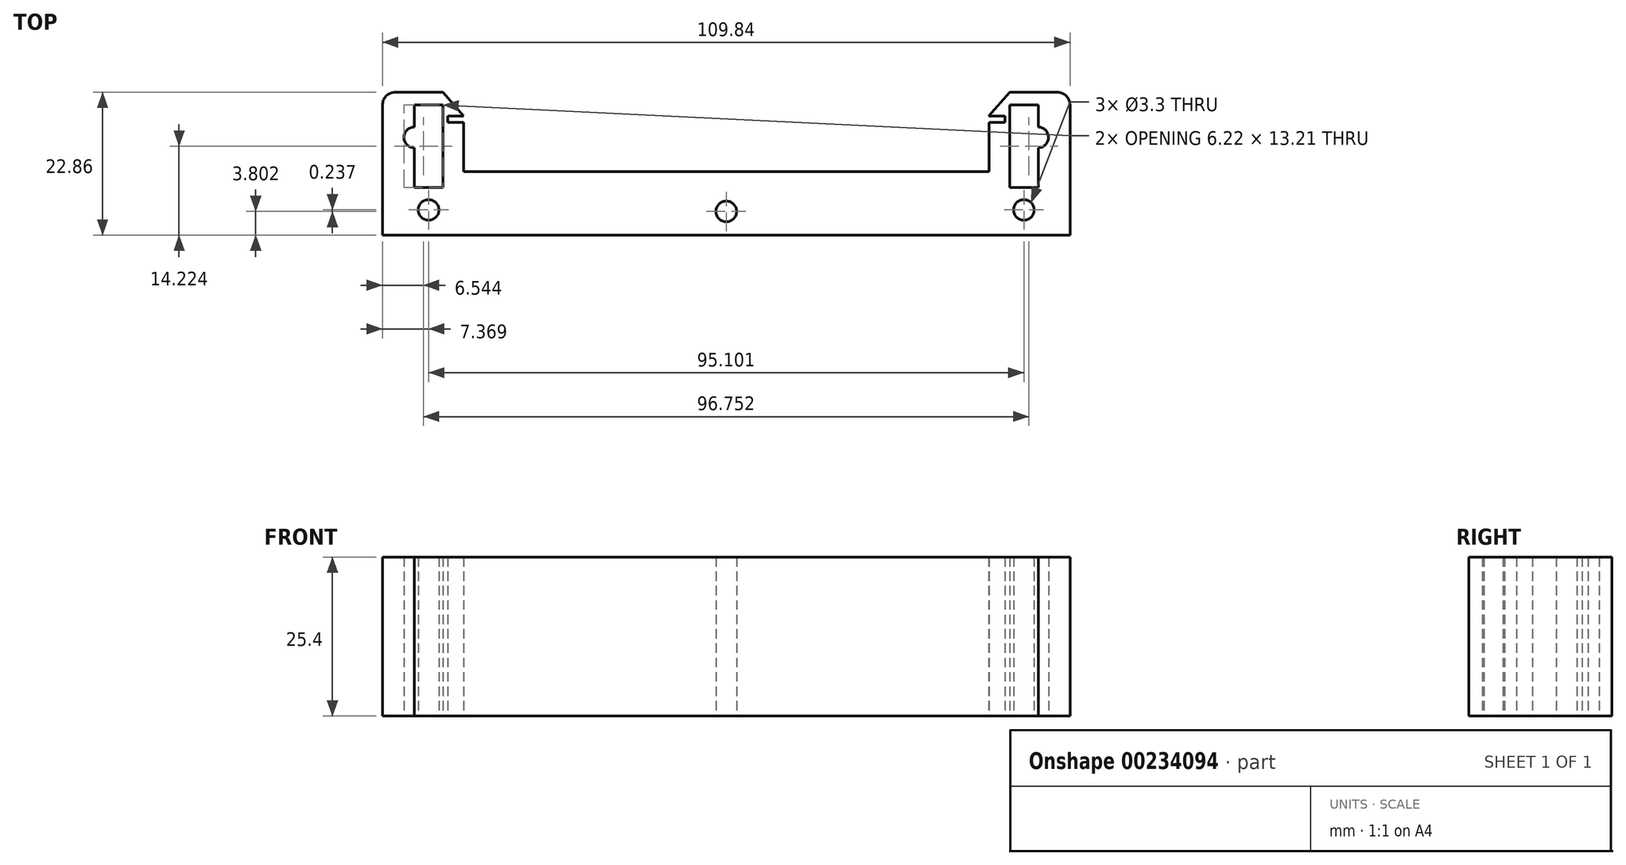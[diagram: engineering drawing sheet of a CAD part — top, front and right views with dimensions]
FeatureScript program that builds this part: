
annotation { "Feature Type Name" : "Feature", "Feature Type Description" : "" }
export const myFeature = defineFeature(function(context is Context, id is Id, definition is map)
    precondition{}
    {
        {
            var Q0;
            Q0=qCreatedBy(makeId("Top.planeOp"),FACE);
            var sketch = newSketch(context, id + "F0", { "sketchPlane" : qUnion([Q0])});
            skLineSegment(sketch, "E0.bottom", {"start": v(-49.84, -11.43) * mm, "end": v(49.84, -11.43) * mm});
            skLineSegment(sketch, "E0.top", {"start": v(-49.84, -19.05) * mm, "end": v(49.84, -19.05) * mm});
            skLineSegment(sketch, "E0.left", {"start": v(-49.84, -11.43) * mm, "end": v(-49.84, -19.05) * mm});
            skLineSegment(sketch, "E1.bottom", {"start": v(-49.84, -11.43) * mm, "end": v(-45.26, -11.43) * mm});
            skLineSegment(sketch, "E1.left", {"start": v(-49.84, -11.43) * mm, "end": v(-49.84, 1.78) * mm});
            skLineSegment(sketch, "E1.right", {"start": v(-45.26, -11.43) * mm, "end": v(-45.26, 3.8) * mm});
            skLineSegment(sketch, "E2.top", {"start": v(-45.26, 0) * mm, "end": v(-41.95, 0) * mm});
            skLineSegment(sketch, "E2.left", {"start": v(-45.26, 3.8) * mm, "end": v(-45.26, 0) * mm});
            skLineSegment(sketch, "E3.bottom", {"start": v(-45.26, -1) * mm, "end": v(-41.96, -1) * mm});
            skLineSegment(sketch, "E3.top", {"start": v(-45.26, -11.43) * mm, "end": v(-41.96, -11.43) * mm});
            skLineSegment(sketch, "E3.left", {"start": v(-45.26, -1) * mm, "end": v(-45.26, -11.43) * mm});
            skLineSegment(sketch, "E3.right", {"start": v(-41.96, -1) * mm, "end": v(-41.96, -11.43) * mm});
            skLineSegment(sketch, "E4", {"start": v(-45.26, 3.8) * mm, "end": v(-41.95, 0) * mm});
            skLineSegment(sketch, "E5.MirrorCS", {"start": v(45.26, -11.43) * mm, "end": v(41.96, -11.43) * mm});
            skLineSegment(sketch, "E6.MirrorCS", {"start": v(41.96, -1) * mm, "end": v(41.96, -11.43) * mm});
            skLineSegment(sketch, "E7.MirrorCS", {"start": v(45.26, -1) * mm, "end": v(41.96, -1) * mm});
            skLineSegment(sketch, "E8.MirrorCS", {"start": v(45.26, -1) * mm, "end": v(45.26, -11.43) * mm});
            skLineSegment(sketch, "E9.MirrorCS", {"start": v(45.26, 0) * mm, "end": v(41.95, 0) * mm});
            skLineSegment(sketch, "E10.MirrorCS", {"start": v(45.26, 3.81) * mm, "end": v(41.95, 0) * mm});
            skLineSegment(sketch, "E11.MirrorCS", {"start": v(45.26, 3.8) * mm, "end": v(45.26, 0) * mm});
            skLineSegment(sketch, "E12.MirrorCS", {"start": v(47.8, 3.8) * mm, "end": v(45.26, 3.8) * mm});
            skLineSegment(sketch, "E13.MirrorCS", {"start": v(49.84, -11.43) * mm, "end": v(49.84, 1.78) * mm});
            skLineSegment(sketch, "E14.MirrorCS", {"start": v(45.26, -11.43) * mm, "end": v(45.26, 3.8) * mm});
            skLineSegment(sketch, "E15.MirrorCS", {"start": v(49.84, -11.43) * mm, "end": v(49.84, -19.05) * mm});
            skPoint(sketch, "E16.visualSharp", {"position": v(-49.84, 3.8) * mm});
            skPoint(sketch, "E17.visualSharp", {"position": v(49.84, 3.8) * mm});
            skCircle(sketch, "E18", {"center": v(-47.55, -15.01) * mm, "radius": 1.65 * mm});
            skPoint(sketch, "E18.centerSnap0", {"position": v(-47.55, -11.43) * mm});
            skCircle(sketch, "E19", {"center": v(-49.84, -3.42) * mm, "radius": 1.65 * mm});
            skCircle(sketch, "E20.MirrorC", {"center": v(49.84, -3.42) * mm, "radius": 1.65 * mm});
            skCircle(sketch, "E21.MirrorC", {"center": v(47.55, -15.01) * mm, "radius": 1.65 * mm});
            skCircle(sketch, "E22", {"center": v(0.01, -15.25) * mm, "radius": 1.65 * mm});
            skLineSegment(sketch, "E23.bottom", {"start": v(-49.84, 1.78) * mm, "end": v(-54.92, 1.78) * mm});
            skLineSegment(sketch, "E23.top", {"start": v(-49.84, -19.05) * mm, "end": v(-54.92, -19.05) * mm});
            skLineSegment(sketch, "E23.left", {"start": v(-49.84, 1.78) * mm, "end": v(-49.84, -19.05) * mm});
            skLineSegment(sketch, "E23.right", {"start": v(-54.92, 1.78) * mm, "end": v(-54.92, -19.05) * mm});
            skLineSegment(sketch, "E24.bottom", {"start": v(-54.92, 1.78) * mm, "end": v(-45.26, 1.78) * mm});
            skLineSegment(sketch, "E24.top", {"start": v(-52.88, 3.8) * mm, "end": v(-45.26, 3.8) * mm});
            skLineSegment(sketch, "E24.left", {"start": v(-54.92, 1.78) * mm, "end": v(-54.92, 1.78) * mm});
            skLineSegment(sketch, "E24.right", {"start": v(-45.26, 1.78) * mm, "end": v(-45.26, 3.8) * mm});
            skLineSegment(sketch, "E25.MirrorCS", {"start": v(54.92, 1.78) * mm, "end": v(54.92, -19.05) * mm});
            skLineSegment(sketch, "E26.MirrorCS", {"start": v(49.84, -19.05) * mm, "end": v(54.92, -19.05) * mm});
            skLineSegment(sketch, "E27.MirrorCS", {"start": v(54.92, 1.78) * mm, "end": v(45.26, 1.78) * mm});
            skLineSegment(sketch, "E28.MirrorCS", {"start": v(52.88, 3.8) * mm, "end": v(45.26, 3.8) * mm});
            skLineSegment(sketch, "E29.MirrorCS", {"start": v(54.92, 1.78) * mm, "end": v(54.92, 1.78) * mm});
            skLineSegment(sketch, "E30.MirrorCS", {"start": v(49.84, 1.78) * mm, "end": v(49.84, -19.05) * mm});
            skPoint(sketch, "E31.visualSharp", {"position": v(-54.92, 3.8) * mm});
            skArc(sketch, "E31.filletArc", {"start": v(-52.88, 3.8) * mm, "mid": v(-54.32, 3.21) * mm, "end": v(-54.92, 1.78) * mm});
            skPoint(sketch, "E32.visualSharp", {"position": v(54.92, 3.8) * mm});
            skArc(sketch, "E32.filletArc", {"start": v(54.92, 1.78) * mm, "mid": v(54.32, 3.21) * mm, "end": v(52.88, 3.8) * mm});
            skLineSegment(sketch, "E33.bottom", {"start": v(-41.96, -11.43) * mm, "end": v(41.96, -11.43) * mm});
            skLineSegment(sketch, "E33.top", {"start": v(-41.96, -8.89) * mm, "end": v(41.96, -8.89) * mm});
            skLineSegment(sketch, "E33.left", {"start": v(-41.96, -11.43) * mm, "end": v(-41.96, -8.89) * mm});
            skLineSegment(sketch, "E33.right", {"start": v(41.96, -11.43) * mm, "end": v(41.96, -8.89) * mm});
            skLineSegment(sketch, "E34.bottom", {"start": v(-45.26, -1) * mm, "end": v(-44.5, -1) * mm});
            skLineSegment(sketch, "E34.top", {"start": v(-45.26, 0) * mm, "end": v(-44.5, 0) * mm});
            skLineSegment(sketch, "E34.left", {"start": v(-45.26, -1) * mm, "end": v(-45.26, 0) * mm});
            skLineSegment(sketch, "E34.right", {"start": v(-44.5, -1) * mm, "end": v(-44.5, 0) * mm});
            skLineSegment(sketch, "E35.MirrorCS", {"start": v(44.5, -1) * mm, "end": v(44.5, 0) * mm});
            skSolve(sketch);
        }
        {
            var Q0;
            Q0 = qSketchRegion(id + "F0", true);
            var Q1;
            {var subQ5=sQuery(id+"F0.wireOp",EDGE,"E1.bottom");Q1=makeQuery(id+"F0.imprint","IMPRINT",FACE,{"disambiguationData":[TD([[makeQuery(id+"F0.imprint","IMPRINT",EDGE,{"derivedFrom":subQ5}),1.0]])]});}
            var Q2;
            {var subQ9=sQuery(id+"F0.wireOp",EDGE,"E0.bottom");Q2=makeQuery(id+"F0.imprint","IMPRINT",FACE,{"disambiguationData":[TD([[makeQuery(id+"F0.imprint","IMPRINT",EDGE,{"derivedFrom":subQ9}),1.0]])]});}
            extrude(context, id + "F1", {"entities" : qUnion([Q0, Q1, Q2]), "depth" : 25.4 * mm});
        }
    });
